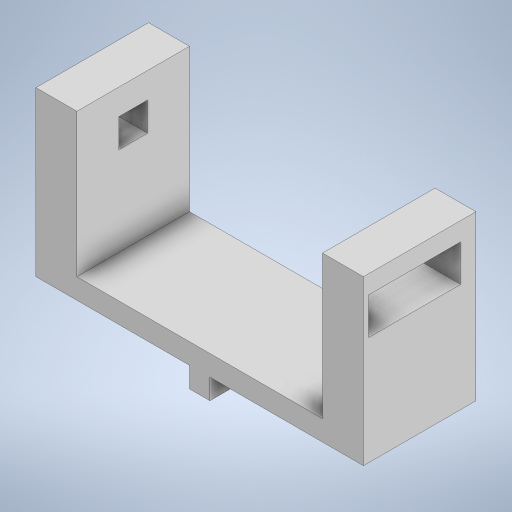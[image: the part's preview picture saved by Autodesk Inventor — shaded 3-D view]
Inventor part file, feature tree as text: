
AUTODESK INVENTOR PART (.ipt)
format: ipt  version: 2023 (Build 270158000, 158)  size: 253,440 bytes
history: native  units: mm
features: extrude x5, sketch x5, other x1
ambient origin geometry x8: Origin, YZ Plane, XZ Plane, XY Plane, X Axis, Y Axis, Z Axis, Center Point
bodies: Body1 (feature_tree)
feature tree (11):
  other  "Sólido1"
  extrude  "Extrusión1"  Depth=10.0mm
  extrude  "Extrusión2"  Depth=20.0mm
  extrude  "Extrusión3"  Depth=70.0mm TaperAngle=0.0deg
  extrude  "Extrusión4"  Depth=14.0mm
  extrude  "Extrusión5"  Depth=12.5mm
  sketch  "Boceto1"  dims[d0=160.0mm d1=10.0mm]
  sketch  "Boceto2"  dims[d2=55.0mm d3=0.0mm d4=20.0mm]
  sketch  "Boceto3"  dims[d5=20.0mm d6=70.0mm d7=0.0mm]
  sketch  "Boceto4"  dims[d10=14.0mm d11=14.0mm]
  sketch  "Boceto5"  dims[d12=20.5mm d13=12.5mm d14=70.0mm d15=0.0mm d17=10.0mm d18=10.0mm d19=0.0mm d20=45.0mm d21=18.0mm d22=9.0mm d23=7.5mm d24=30.0mm d25=0.0mm]
